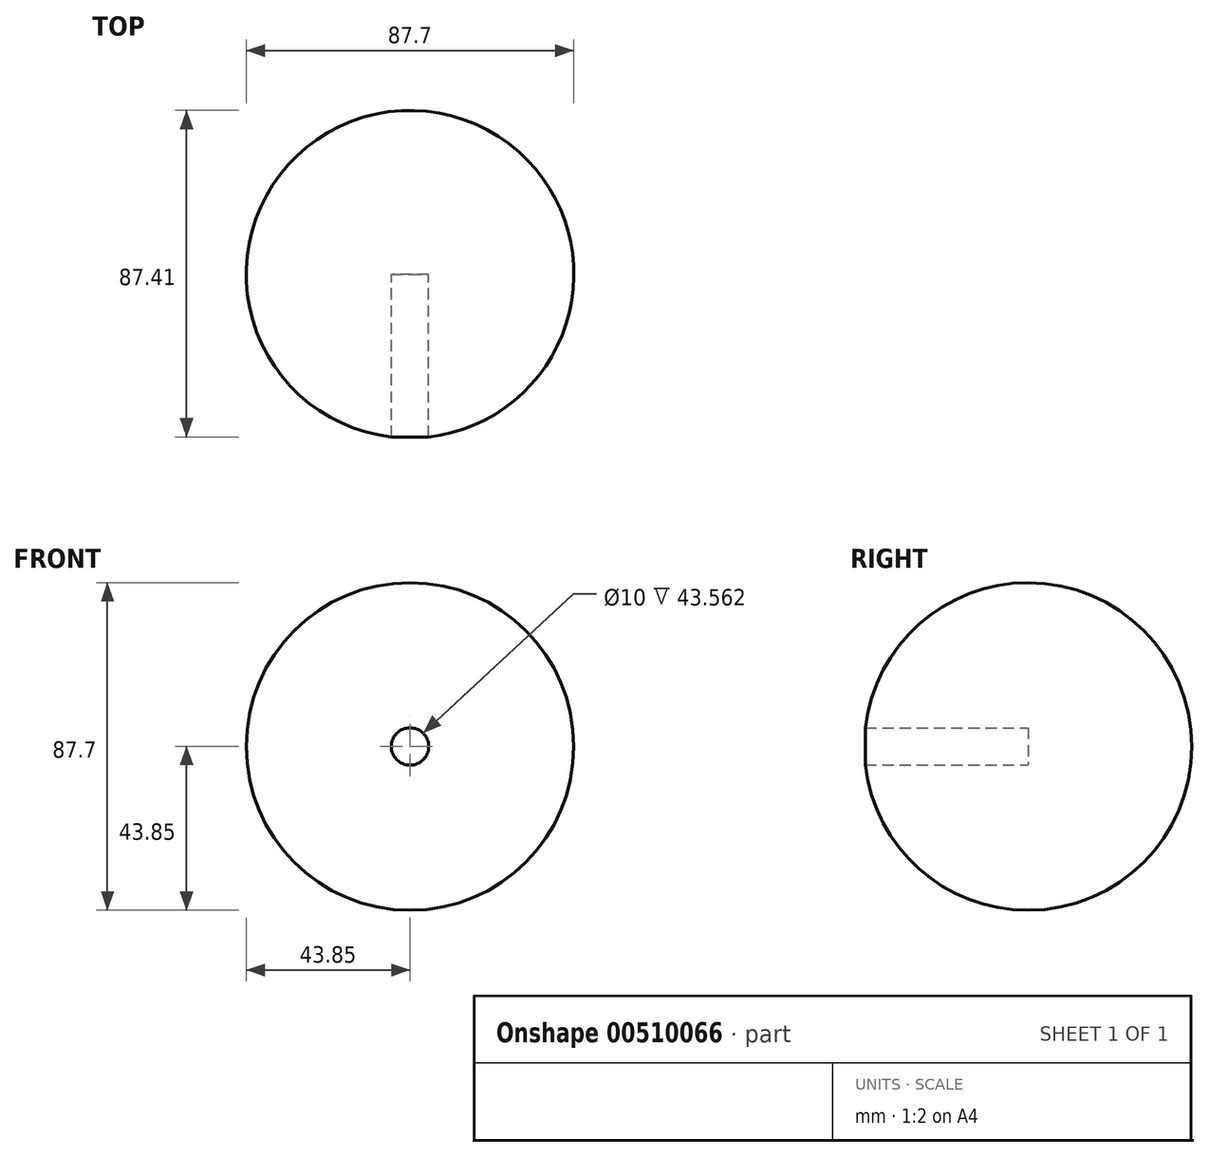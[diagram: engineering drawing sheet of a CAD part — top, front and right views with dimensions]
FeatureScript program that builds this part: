
annotation { "Feature Type Name" : "Feature", "Feature Type Description" : "" }
export const myFeature = defineFeature(function(context is Context, id is Id, definition is map)
    precondition{}
    {
        {
            var Q0;
            Q0=qCreatedBy(makeId("Front.planeOp"),FACE);
            var sketch = newSketch(context, id + "F0", { "sketchPlane" : qUnion([Q0])});
            skLineSegment(sketch, "E0", {"start": v(0, -43.85) * mm, "end": v(0, 43.85) * mm});
            skArc(sketch, "E1", {"start": v(0, -43.85) * mm, "mid": v(43.85, 0) * mm, "end": v(0, 43.85) * mm});
            skSolve(sketch);
        }
        {
            var Q0;
            Q0=makeQuery(id+"F0.imprint","IMPRINT",FACE,{"disambiguationData":[TD([[makeQuery(id+"F0.imprint","IMPRINT",EDGE,{"derivedFrom":sQuery(id+"F0.wireOp",EDGE,"E0")}),-1.0]])]});
            var Q1;
            Q1=sQuery(id+"F0.wireOp",EDGE,"E0");
            revolve(context, id + "F1", {"entities" : qUnion([Q0]), "axis" : qUnion([Q1]), "revolveType" : RevolveType.FULL});
        }
        {
            var Q0;
            Q0=sQuery(id+"F0.wireOp",VERTEX,"E1.center");
            var Q1;
            Q1=makeQuery(id+"F1.opRevolve","SWEPT_BODY",BODY,{"disambiguationData":[OSD([sQuery(id+"F0.wireOp",EDGE,"E0"),sQuery(id+"F0.wireOp",EDGE,"E1")])]});
            hole(context, id + "F2", {"style" : HoleStyle.SIMPLE, "endStyle" : HoleEndStyle.BLIND, "oppositeDirection" : true, "holeDiameter" : 10 * mm, "holeDepth" : 100 * mm, "isTappedThrough" : true, "tappedDepth" : 12.7 * mm, "tapClearance" : 3, "locations" : qUnion([Q0]), "scope" : qUnion([Q1])});
        }
    });
